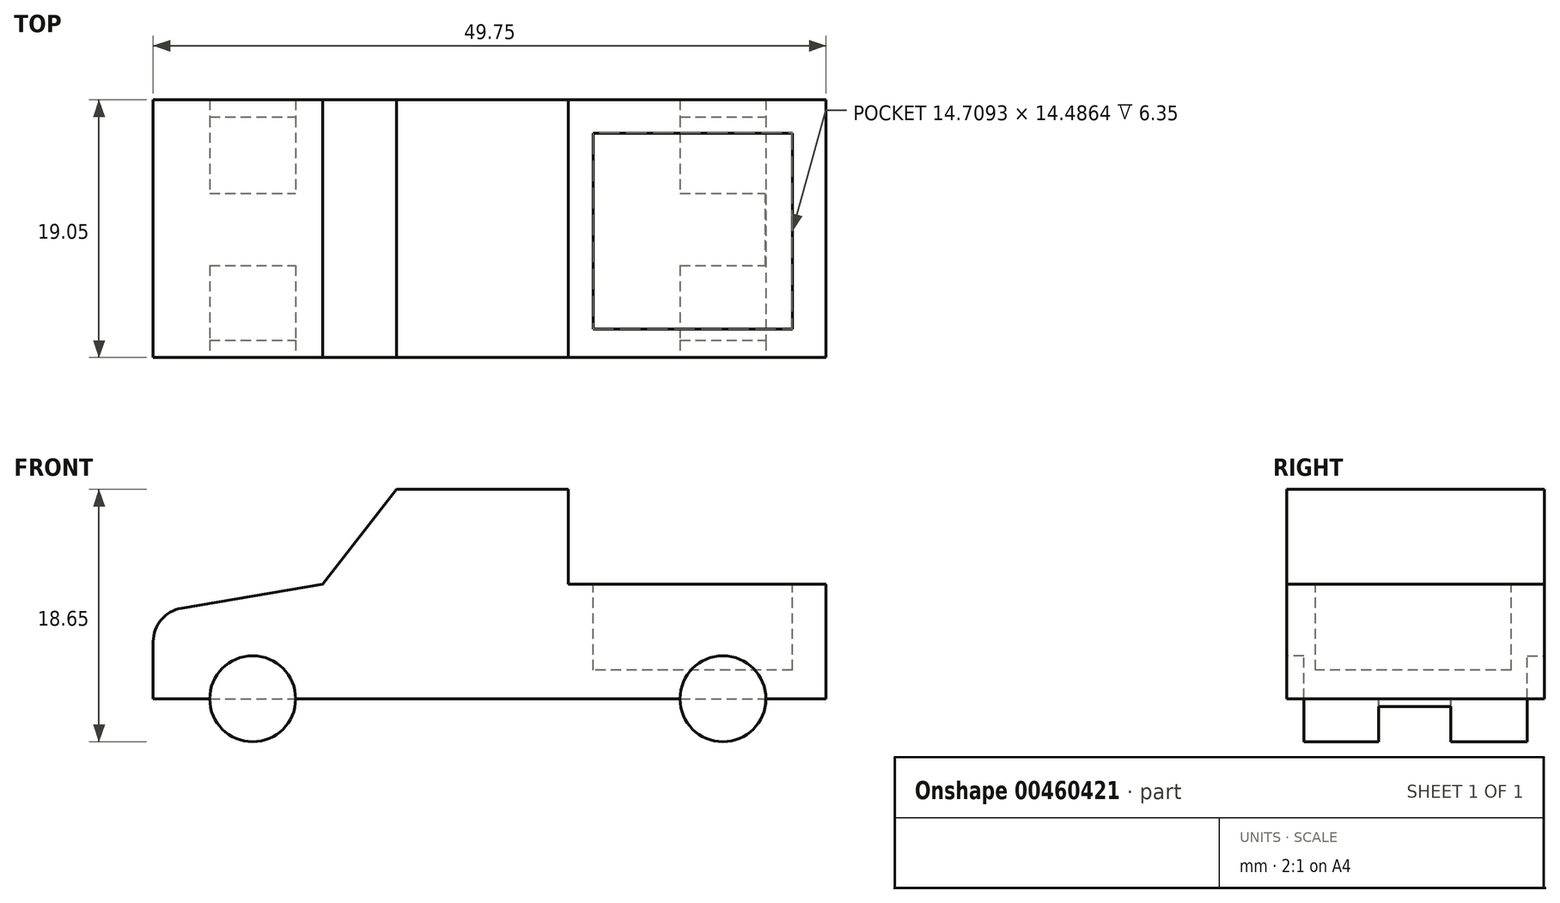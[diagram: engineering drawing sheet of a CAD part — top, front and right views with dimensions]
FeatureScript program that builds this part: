
annotation { "Feature Type Name" : "Feature", "Feature Type Description" : "" }
export const myFeature = defineFeature(function(context is Context, id is Id, definition is map)
    precondition{}
    {
        {
            var Q0;
            Q0=qCreatedBy(makeId("Front.planeOp"),FACE);
            var sketch = newSketch(context, id + "F0", { "sketchPlane" : qUnion([Q0])});
            skLineSegment(sketch, "E0", {"start": v(0, 0) * mm, "end": v(0, 6.35) * mm});
            skLineSegment(sketch, "E1", {"start": v(0, 6.35) * mm, "end": v(12.52, 8.48) * mm});
            skLineSegment(sketch, "E2", {"start": v(12.52, 8.48) * mm, "end": v(18, 15.48) * mm});
            skLineSegment(sketch, "E3", {"start": v(18, 15.48) * mm, "end": v(30.7, 15.48) * mm});
            skLineSegment(sketch, "E4", {"start": v(30.7, 15.48) * mm, "end": v(30.7, 8.48) * mm});
            skLineSegment(sketch, "E5", {"start": v(30.7, 8.48) * mm, "end": v(49.75, 8.48) * mm});
            skLineSegment(sketch, "E6", {"start": v(49.75, 8.48) * mm, "end": v(49.75, 0) * mm});
            skLineSegment(sketch, "E7", {"start": v(49.75, 0) * mm, "end": v(0, 0) * mm});
            skSolve(sketch);
        }
        {
            var Q0;
            Q0=makeQuery(id+"F0.imprint","IMPRINT",FACE,{"disambiguationData":[TD([[makeQuery(id+"F0.imprint","IMPRINT",EDGE,{"derivedFrom":sQuery(id+"F0.wireOp",EDGE,"E0")}),-1.0]])]});
            extrude(context, id + "F1", {"entities" : qUnion([Q0]), "depth" : 19.05 * mm});
        }
        {
            var Q0;
            Q0=makeQuery(id+"F1.opExtrude","CAP_FACE",FACE,{"disambiguationData":[OSD([sQuery(id+"F0.wireOp",EDGE,"E0"),sQuery(id+"F0.wireOp",EDGE,"E1"),sQuery(id+"F0.wireOp",EDGE,"E2"),sQuery(id+"F0.wireOp",EDGE,"E3"),sQuery(id+"F0.wireOp",EDGE,"E4"),sQuery(id+"F0.wireOp",EDGE,"E5"),sQuery(id+"F0.wireOp",EDGE,"E6"),sQuery(id+"F0.wireOp",EDGE,"E7")])],"isStart":false});
            var sketch = newSketch(context, id + "F2", { "sketchPlane" : qUnion([Q0])});
            skCircle(sketch, "E8", {"center": v(7.35, 0) * mm, "radius": 3.18 * mm});
            skSolve(sketch);
        }
        {
            var Q0;
            {var subQ0=makeQuery(id+"F1.opExtrude","CAP_EDGE",EDGE,{"disambiguationData":[OSD([sQuery(id+"F0.wireOp",EDGE,"E0")])],"isStart":false});Q0=makeQuery(id+"F2.imprint","IMPRINT",FACE,{"disambiguationData":[TD([[makeQuery(id+"F2.imprint","IMPRINT",EDGE,{"derivedFrom":subQ0}),-1.0]])]});}
            var sketch = newSketch(context, id + "F3", { "sketchPlane" : qUnion([Q0])});
            skCircle(sketch, "E9", {"center": v(42.12, 0) * mm, "radius": 3.18 * mm});
            skSolve(sketch);
        }
        {
            var Q0;
            {var subQ0=sQuery(id+"F2.wireOp",EDGE,"E8");var subQ1=makeQuery(id+"F1.opExtrude","CAP_EDGE",EDGE,{"disambiguationData":[OSD([sQuery(id+"F0.wireOp",EDGE,"E7")])],"isStart":false});var subQ2=makeQuery(id+"F2.imprint","INTERSECT",VERTEX,{"disambiguationData":[OD(0.0)],"derivedFrom":[subQ1,subQ0]});Q0=makeQuery(id+"F2.imprint","IMPRINT",FACE,{"disambiguationData":[TD([[makeQuery(id+"F2.imprint","IMPRINT",EDGE,{"disambiguationData":[TD([[subQ2,1.0]])],"derivedFrom":subQ0}),1.0]])]});}
            var Q1;
            {var subQ0=sQuery(id+"F2.wireOp",EDGE,"E8");var subQ1=makeQuery(id+"F1.opExtrude","CAP_EDGE",EDGE,{"disambiguationData":[OSD([sQuery(id+"F0.wireOp",EDGE,"E7")])],"isStart":false});var subQ2=makeQuery(id+"F2.imprint","INTERSECT",VERTEX,{"disambiguationData":[OD(0.0)],"derivedFrom":[subQ1,subQ0]});Q1=makeQuery(id+"F2.imprint","IMPRINT",FACE,{"disambiguationData":[TD([[makeQuery(id+"F2.imprint","IMPRINT",EDGE,{"disambiguationData":[TD([[subQ2,-1.0]])],"derivedFrom":subQ0}),1.0]])]});}
            var Q2;
            {var subQ0=sQuery(id+"F3.wireOp",EDGE,"E9");var subQ1=makeQuery(id+"F1.opExtrude","CAP_EDGE",EDGE,{"disambiguationData":[OSD([sQuery(id+"F0.wireOp",EDGE,"E7")])],"isStart":false});var subQ2=makeQuery(id+"F2.imprint","IMPRINT",EDGE,{"disambiguationData":[TD([[makeQuery(id+"F2.imprint","INTERSECT",VERTEX,{"derivedFrom":[makeQuery(id+"F1.opExtrude","CAP_EDGE",EDGE,{"disambiguationData":[OSD([sQuery(id+"F0.wireOp",EDGE,"E6")])],"isStart":false}),subQ1]}),-1.0]])],"derivedFrom":subQ1});var subQ3=makeQuery(id+"F3.imprint","INTERSECT",VERTEX,{"disambiguationData":[OD(0.0)],"derivedFrom":[subQ2,subQ0]});Q2=makeQuery(id+"F3.imprint","IMPRINT",FACE,{"disambiguationData":[TD([[makeQuery(id+"F3.imprint","IMPRINT",EDGE,{"disambiguationData":[TD([[subQ3,1.0]])],"derivedFrom":subQ0}),1.0]])]});}
            extrude(context, id + "F4", {"entities" : qUnion([Q0, Q1, Q2]), "operationType" : NewBodyOperationType.ADD, "oppositeDirection" : true, "depth" : 19.05 * mm});
        }
        {
            var Q0;
            Q0=makeQuery(id+"F1.opExtrude","SWEPT_EDGE",EDGE,{"disambiguationData":[OSD([sQuery(id+"F0.wireOp",EDGE,"E0"),sQuery(id+"F0.wireOp",EDGE,"E1")])]});
            fillet(context, id + "F5", {"entities" : qUnion([Q0]), "radius" : 2.54 * mm, "tangentPropagation" : true, "allowEdgeOverflow" : false});
        }
        {
            var Q0;
            {var subQ0=sQuery(id+"F0.wireOp",EDGE,"E7");Q0=makeQuery(id+"F4.boolean.opBoolean","MERGE",FACE,{"derivedFrom":[makeQuery(id+"F1.opExtrude","CAP_FACE",FACE,{"disambiguationData":[OSD([sQuery(id+"F0.wireOp",EDGE,"E0"),sQuery(id+"F0.wireOp",EDGE,"E1"),sQuery(id+"F0.wireOp",EDGE,"E2"),sQuery(id+"F0.wireOp",EDGE,"E3"),sQuery(id+"F0.wireOp",EDGE,"E4"),sQuery(id+"F0.wireOp",EDGE,"E5"),sQuery(id+"F0.wireOp",EDGE,"E6"),subQ0])],"isStart":true}),makeQuery(id+"F4.opExtrude","CAP_FACE",FACE,{"disambiguationData":[OSD([sQuery(id+"F2.wireOp",EDGE,"E8")])],"isStart":false}),makeQuery(id+"F4.opExtrude","CAP_FACE",FACE,{"disambiguationData":[OSD([subQ0,sQuery(id+"F3.wireOp",EDGE,"E9")])],"isStart":false})]});}
            var sketch = newSketch(context, id + "F6", { "sketchPlane" : qUnion([Q0])});
            skCircle(sketch, "E10", {"center": v(-7.35, 0) * mm, "radius": 3.18 * mm});
            skSolve(sketch);
        }
        {
            var Q0;
            {var subQ0=sQuery(id+"F6.wireOp",EDGE,"E10");Q0=makeQuery(id+"F6.imprint","IMPRINT",FACE,{"disambiguationData":[TD([[makeQuery(id+"F6.imprint","IMPRINT",EDGE,{"disambiguationData":[OD(0.0)],"derivedFrom":subQ0}),1.0]])]});}
            extrude(context, id + "F7", {"entities" : qUnion([Q0]), "operationType" : NewBodyOperationType.ADD, "oppositeDirection" : true, "depth" : 1.27 * mm});
        }
        {
            var Q0;
            {var subQ0=sQuery(id+"F0.wireOp",EDGE,"E7");Q0=makeQuery(id+"F4.boolean.opBoolean","MERGE",FACE,{"derivedFrom":[makeQuery(id+"F1.opExtrude","CAP_FACE",FACE,{"disambiguationData":[OSD([sQuery(id+"F0.wireOp",EDGE,"E0"),sQuery(id+"F0.wireOp",EDGE,"E1"),sQuery(id+"F0.wireOp",EDGE,"E2"),sQuery(id+"F0.wireOp",EDGE,"E3"),sQuery(id+"F0.wireOp",EDGE,"E4"),sQuery(id+"F0.wireOp",EDGE,"E5"),sQuery(id+"F0.wireOp",EDGE,"E6"),subQ0])],"isStart":true}),makeQuery(id+"F4.opExtrude","CAP_FACE",FACE,{"disambiguationData":[OSD([sQuery(id+"F2.wireOp",EDGE,"E8")])],"isStart":false}),makeQuery(id+"F4.opExtrude","CAP_FACE",FACE,{"disambiguationData":[OSD([subQ0,sQuery(id+"F3.wireOp",EDGE,"E9")])],"isStart":false})]});}
            var sketch = newSketch(context, id + "F8", { "sketchPlane" : qUnion([Q0])});
            skCircle(sketch, "E11", {"center": v(-7.35, 0) * mm, "radius": 3.18 * mm});
            skSolve(sketch);
        }
        {
            var Q0;
            {var subQ0=sQuery(id+"F8.wireOp",EDGE,"E11");Q0=makeQuery(id+"F8.imprint","IMPRINT",FACE,{"disambiguationData":[TD([[makeQuery(id+"F8.imprint","IMPRINT",EDGE,{"disambiguationData":[OD(0.0)],"derivedFrom":subQ0}),1.0]])]});}
            extrude(context, id + "F9", {"entities" : qUnion([Q0]), "operationType" : NewBodyOperationType.REMOVE, "oppositeDirection" : true, "depth" : 1.27 * mm});
        }
        {
            var Q0;
            {var subQ0=sQuery(id+"F0.wireOp",EDGE,"E7");Q0=makeQuery(id+"F4.boolean.opBoolean","MERGE",FACE,{"derivedFrom":[makeQuery(id+"F1.opExtrude","CAP_FACE",FACE,{"disambiguationData":[OSD([sQuery(id+"F0.wireOp",EDGE,"E0"),sQuery(id+"F0.wireOp",EDGE,"E1"),sQuery(id+"F0.wireOp",EDGE,"E2"),sQuery(id+"F0.wireOp",EDGE,"E3"),sQuery(id+"F0.wireOp",EDGE,"E4"),sQuery(id+"F0.wireOp",EDGE,"E5"),sQuery(id+"F0.wireOp",EDGE,"E6"),subQ0])],"isStart":true}),makeQuery(id+"F4.opExtrude","CAP_FACE",FACE,{"disambiguationData":[OSD([sQuery(id+"F2.wireOp",EDGE,"E8")])],"isStart":false}),makeQuery(id+"F4.opExtrude","CAP_FACE",FACE,{"disambiguationData":[OSD([subQ0,sQuery(id+"F3.wireOp",EDGE,"E9")])],"isStart":false})]});}
            var sketch = newSketch(context, id + "F10", { "sketchPlane" : qUnion([Q0])});
            skCircle(sketch, "E12", {"center": v(-42.12, 0) * mm, "radius": 3.18 * mm});
            skSolve(sketch);
        }
        {
            var Q0;
            {var subQ0=sQuery(id+"F10.wireOp",EDGE,"E12");Q0=makeQuery(id+"F10.imprint","IMPRINT",FACE,{"disambiguationData":[TD([[makeQuery(id+"F10.imprint","IMPRINT",EDGE,{"disambiguationData":[OD(0.0)],"derivedFrom":subQ0}),1.0]])]});}
            extrude(context, id + "F11", {"entities" : qUnion([Q0]), "operationType" : NewBodyOperationType.REMOVE, "oppositeDirection" : true, "depth" : 1.27 * mm});
        }
        {
            var Q0;
            {var subQ0=sQuery(id+"F0.wireOp",EDGE,"E7");Q0=makeQuery(id+"F4.boolean.opBoolean","MERGE",FACE,{"derivedFrom":[makeQuery(id+"F1.opExtrude","CAP_FACE",FACE,{"disambiguationData":[OSD([sQuery(id+"F0.wireOp",EDGE,"E0"),sQuery(id+"F0.wireOp",EDGE,"E1"),sQuery(id+"F0.wireOp",EDGE,"E2"),sQuery(id+"F0.wireOp",EDGE,"E3"),sQuery(id+"F0.wireOp",EDGE,"E4"),sQuery(id+"F0.wireOp",EDGE,"E5"),sQuery(id+"F0.wireOp",EDGE,"E6"),subQ0])],"isStart":false}),makeQuery(id+"F4.opExtrude","CAP_FACE",FACE,{"disambiguationData":[OSD([sQuery(id+"F2.wireOp",EDGE,"E8")])],"isStart":true}),makeQuery(id+"F4.opExtrude","CAP_FACE",FACE,{"disambiguationData":[OSD([subQ0,sQuery(id+"F3.wireOp",EDGE,"E9")])],"isStart":true})]});}
            var sketch = newSketch(context, id + "F12", { "sketchPlane" : qUnion([Q0])});
            skCircle(sketch, "E13", {"center": v(42.12, 0) * mm, "radius": 3.18 * mm});
            skCircle(sketch, "E14", {"center": v(7.35, 0) * mm, "radius": 3.18 * mm});
            skSolve(sketch);
        }
        {
            var Q0;
            {var subQ0=sQuery(id+"F12.wireOp",EDGE,"E13");var subQ1=sQuery(id+"F2.wireOp",EDGE,"E8");var subQ2=makeQuery(id+"F4.opExtrude","CAP_FACE",FACE,{"disambiguationData":[OSD([subQ1])],"isStart":true});var subQ3=sQuery(id+"F0.wireOp",EDGE,"E7");var subQ4=makeQuery(id+"F1.opExtrude","SWEPT_FACE",FACE,{"disambiguationData":[OSD([subQ3])]});var subQ5=sQuery(id+"F0.wireOp",EDGE,"E6");var subQ6=makeQuery(id+"F1.opExtrude","CAP_FACE",FACE,{"disambiguationData":[OSD([sQuery(id+"F0.wireOp",EDGE,"E0"),sQuery(id+"F0.wireOp",EDGE,"E1"),sQuery(id+"F0.wireOp",EDGE,"E2"),sQuery(id+"F0.wireOp",EDGE,"E3"),sQuery(id+"F0.wireOp",EDGE,"E4"),sQuery(id+"F0.wireOp",EDGE,"E5"),subQ5,subQ3])],"isStart":false});var subQ7=sQuery(id+"F3.wireOp",EDGE,"E9");var subQ8=makeQuery(id+"F4.opExtrude","CAP_FACE",FACE,{"disambiguationData":[OSD([subQ3,subQ7])],"isStart":true});var subQ9=makeQuery(id+"F4.opExtrude","SWEPT_FACE",FACE,{"disambiguationData":[OSD([subQ7])]});var subQ10=makeQuery(id+"F1.opExtrude","CAP_EDGE",EDGE,{"disambiguationData":[OSD([subQ3])],"isStart":false});var subQ11=makeQuery(id+"F12.imprint","INTERSECT",VERTEX,{"derivedFrom":[makeQuery(id+"F4.boolean.opBoolean","SPLIT",EDGE,{"disambiguationData":[TD([subQ6,makeQuery(id+"F1.opExtrude","SWEPT_FACE",FACE,{"disambiguationData":[OSD([subQ5])]}),subQ4,subQ2,subQ9,subQ8])],"derivedFrom":subQ10}),subQ0]});Q0=makeQuery(id+"F12.imprint","IMPRINT",FACE,{"disambiguationData":[TD([[makeQuery(id+"F12.imprint","IMPRINT",EDGE,{"disambiguationData":[TD([[subQ11,-1.0]])],"derivedFrom":subQ0}),1.0]])]});}
            var Q1;
            {var subQ0=sQuery(id+"F12.wireOp",EDGE,"E14");var subQ1=sQuery(id+"F0.wireOp",EDGE,"E7");var subQ2=makeQuery(id+"F1.opExtrude","SWEPT_FACE",FACE,{"disambiguationData":[OSD([subQ1])]});var subQ3=sQuery(id+"F2.wireOp",EDGE,"E8");var subQ4=makeQuery(id+"F4.opExtrude","SWEPT_FACE",FACE,{"disambiguationData":[OSD([subQ3])]});var subQ5=sQuery(id+"F0.wireOp",EDGE,"E0");var subQ6=makeQuery(id+"F1.opExtrude","CAP_FACE",FACE,{"disambiguationData":[OSD([subQ5,sQuery(id+"F0.wireOp",EDGE,"E1"),sQuery(id+"F0.wireOp",EDGE,"E2"),sQuery(id+"F0.wireOp",EDGE,"E3"),sQuery(id+"F0.wireOp",EDGE,"E4"),sQuery(id+"F0.wireOp",EDGE,"E5"),sQuery(id+"F0.wireOp",EDGE,"E6"),subQ1])],"isStart":false});var subQ7=sQuery(id+"F3.wireOp",EDGE,"E9");var subQ8=makeQuery(id+"F4.opExtrude","CAP_FACE",FACE,{"disambiguationData":[OSD([subQ1,subQ7])],"isStart":true});var subQ9=makeQuery(id+"F4.opExtrude","CAP_FACE",FACE,{"disambiguationData":[OSD([subQ3])],"isStart":true});var subQ10=makeQuery(id+"F1.opExtrude","CAP_EDGE",EDGE,{"disambiguationData":[OSD([subQ1])],"isStart":false});var subQ11=makeQuery(id+"F12.imprint","INTERSECT",VERTEX,{"derivedFrom":[makeQuery(id+"F4.boolean.opBoolean","SPLIT",EDGE,{"disambiguationData":[TD([makeQuery(id+"F1.opExtrude","SWEPT_FACE",FACE,{"disambiguationData":[OSD([subQ5])]}),subQ6,subQ2,subQ4,subQ9,subQ8])],"derivedFrom":subQ10}),subQ0]});Q1=makeQuery(id+"F12.imprint","IMPRINT",FACE,{"disambiguationData":[TD([[makeQuery(id+"F12.imprint","IMPRINT",EDGE,{"disambiguationData":[TD([[subQ11,1.0]])],"derivedFrom":subQ0}),1.0]])]});}
            extrude(context, id + "F13", {"entities" : qUnion([Q0, Q1]), "operationType" : NewBodyOperationType.REMOVE, "oppositeDirection" : true, "depth" : 1.27 * mm});
        }
        {
            var Q0;
            {var subQ0=sQuery(id+"F0.wireOp",EDGE,"E7");var subQ1=sQuery(id+"F0.wireOp",EDGE,"E6");var subQ2=sQuery(id+"F0.wireOp",EDGE,"E5");var subQ3=sQuery(id+"F0.wireOp",EDGE,"E4");var subQ4=sQuery(id+"F0.wireOp",EDGE,"E3");var subQ5=sQuery(id+"F0.wireOp",EDGE,"E2");var subQ6=sQuery(id+"F0.wireOp",EDGE,"E1");var subQ7=sQuery(id+"F0.wireOp",EDGE,"E0");var subQ8=sQuery(id+"F3.wireOp",EDGE,"E9");var subQ9=sQuery(id+"F2.wireOp",EDGE,"E8");Q0=makeQuery(id+"F4.boolean.opBoolean","SPLIT",FACE,{"disambiguationData":[TD([makeQuery(id+"F1.opExtrude","SWEPT_FACE",FACE,{"disambiguationData":[OSD([subQ7])]}),makeQuery(id+"F1.opExtrude","CAP_FACE",FACE,{"disambiguationData":[OSD([subQ7,subQ6,subQ5,subQ4,subQ3,subQ2,subQ1,subQ0])],"isStart":true}),makeQuery(id+"F1.opExtrude","CAP_FACE",FACE,{"disambiguationData":[OSD([subQ7,subQ6,subQ5,subQ4,subQ3,subQ2,subQ1,subQ0])],"isStart":false}),makeQuery(id+"F4.opExtrude","SWEPT_FACE",FACE,{"disambiguationData":[OSD([subQ9])]}),makeQuery(id+"F4.opExtrude","CAP_FACE",FACE,{"disambiguationData":[OSD([subQ9])],"isStart":true}),makeQuery(id+"F4.opExtrude","CAP_FACE",FACE,{"disambiguationData":[OSD([subQ9])],"isStart":false}),makeQuery(id+"F4.opExtrude","CAP_FACE",FACE,{"disambiguationData":[OSD([subQ0,subQ8])],"isStart":true}),makeQuery(id+"F4.opExtrude","CAP_FACE",FACE,{"disambiguationData":[OSD([subQ0,subQ8])],"isStart":false})])],"derivedFrom":makeQuery(id+"F1.opExtrude","SWEPT_FACE",FACE,{"disambiguationData":[OSD([subQ0])]})});}
            var sketch = newSketch(context, id + "F14", { "sketchPlane" : qUnion([Q0])});
            skLineSegment(sketch, "E15.bottom", {"start": v(4.18, 12.26) * mm, "end": v(45.24, 12.26) * mm});
            skLineSegment(sketch, "E15.top", {"start": v(4.18, 6.9) * mm, "end": v(45.24, 6.9) * mm});
            skLineSegment(sketch, "E15.left", {"start": v(4.18, 12.26) * mm, "end": v(4.18, 6.9) * mm});
            skLineSegment(sketch, "E15.right", {"start": v(45.24, 12.26) * mm, "end": v(45.24, 6.9) * mm});
            skSolve(sketch);
        }
        {
            var Q0;
            Q0=makeQuery(id+"F14.imprint","IMPRINT",FACE,{"disambiguationData":[TD([[makeQuery(id+"F14.imprint","IMPRINT",EDGE,{"derivedFrom":sQuery(id+"F14.wireOp",EDGE,"E15.bottom")}),-1.0]])]});
            extrude(context, id + "F15", {"entities" : qUnion([Q0]), "operationType" : NewBodyOperationType.REMOVE, "depth" : 22.6 * mm});
        }
        {
            var Q0;
            Q0=makeQuery(id+"F1.opExtrude","SWEPT_FACE",FACE,{"disambiguationData":[OSD([sQuery(id+"F0.wireOp",EDGE,"E5")])]});
            var sketch = newSketch(context, id + "F16", { "sketchPlane" : qUnion([Q0])});
            skLineSegment(sketch, "E16.bottom", {"start": v(47.25, -2.45) * mm, "end": v(32.54, -2.45) * mm});
            skLineSegment(sketch, "E16.top", {"start": v(47.25, -16.94) * mm, "end": v(32.54, -16.94) * mm});
            skLineSegment(sketch, "E16.left", {"start": v(47.25, -2.45) * mm, "end": v(47.25, -16.94) * mm});
            skLineSegment(sketch, "E16.right", {"start": v(32.54, -2.45) * mm, "end": v(32.54, -16.94) * mm});
            skSolve(sketch);
        }
        {
            var Q0;
            Q0=makeQuery(id+"F16.imprint","IMPRINT",FACE,{"disambiguationData":[TD([[makeQuery(id+"F16.imprint","IMPRINT",EDGE,{"derivedFrom":sQuery(id+"F16.wireOp",EDGE,"E16.bottom")}),1.0]])]});
            extrude(context, id + "F17", {"entities" : qUnion([Q0]), "operationType" : NewBodyOperationType.REMOVE, "oppositeDirection" : true, "depth" : 6.35 * mm});
        }
    });
